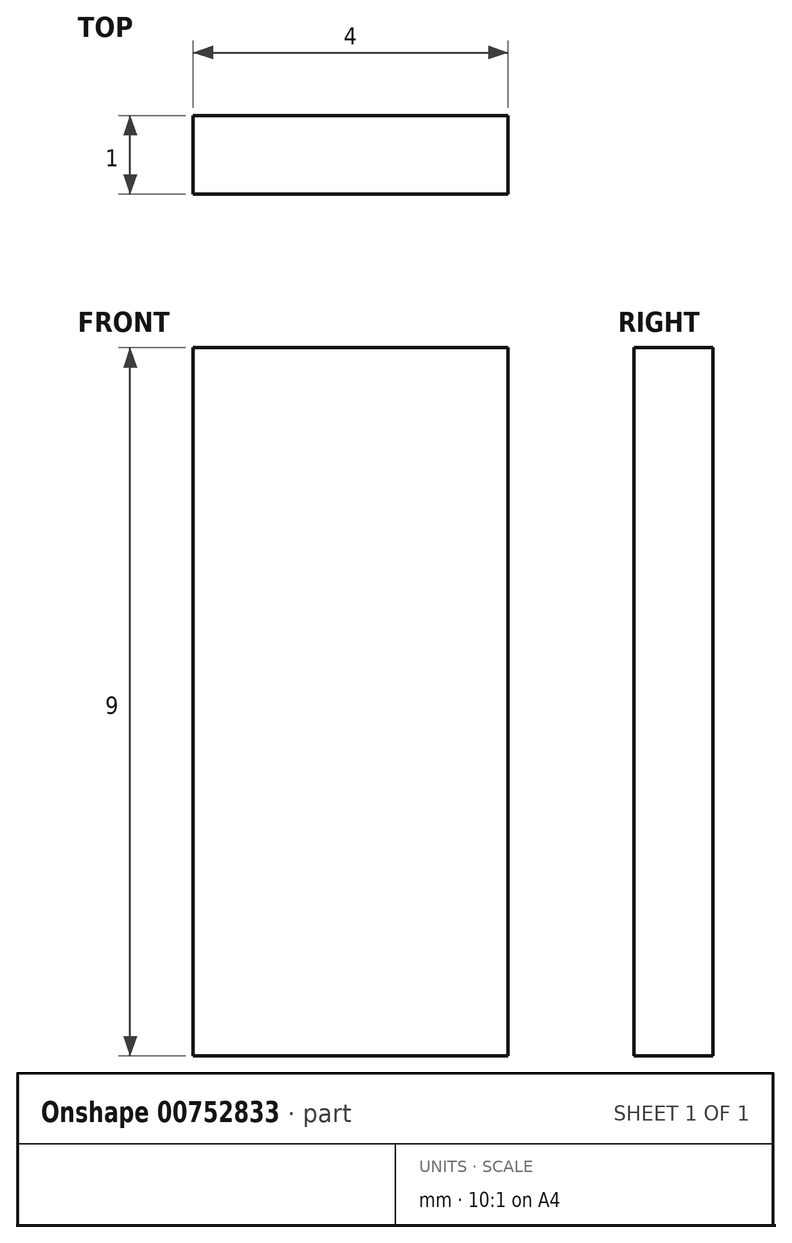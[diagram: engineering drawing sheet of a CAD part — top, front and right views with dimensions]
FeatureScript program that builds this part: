
annotation { "Feature Type Name" : "Feature", "Feature Type Description" : "" }
export const myFeature = defineFeature(function(context is Context, id is Id, definition is map)
    precondition{}
    {
        {
            var Q0;
            Q0=qCreatedBy(makeId("Front.planeOp"),FACE);
            var sketch = newSketch(context, id + "F0", { "sketchPlane" : qUnion([Q0])});
            skLineSegment(sketch, "E0.bottom", {"start": v(-2, 4.5) * mm, "end": v(2, 4.5) * mm});
            skLineSegment(sketch, "E0.top", {"start": v(-2, -4.5) * mm, "end": v(2, -4.5) * mm});
            skLineSegment(sketch, "E0.left", {"start": v(-2, 4.5) * mm, "end": v(-2, -4.5) * mm});
            skLineSegment(sketch, "E0.right", {"start": v(2, 4.5) * mm, "end": v(2, -4.5) * mm});
            skSolve(sketch);
        }
        {
            var Q0;
            Q0=makeQuery(id+"F0.imprint","IMPRINT",FACE,{"disambiguationData":[TD([[makeQuery(id+"F0.imprint","IMPRINT",EDGE,{"derivedFrom":sQuery(id+"F0.wireOp",EDGE,"E0.bottom")}),-1.0]])]});
            extrude(context, id + "F1", {"entities" : qUnion([Q0]), "depth" : 1 * mm, "offsetDistance" : 25 * mm});
        }
    });
